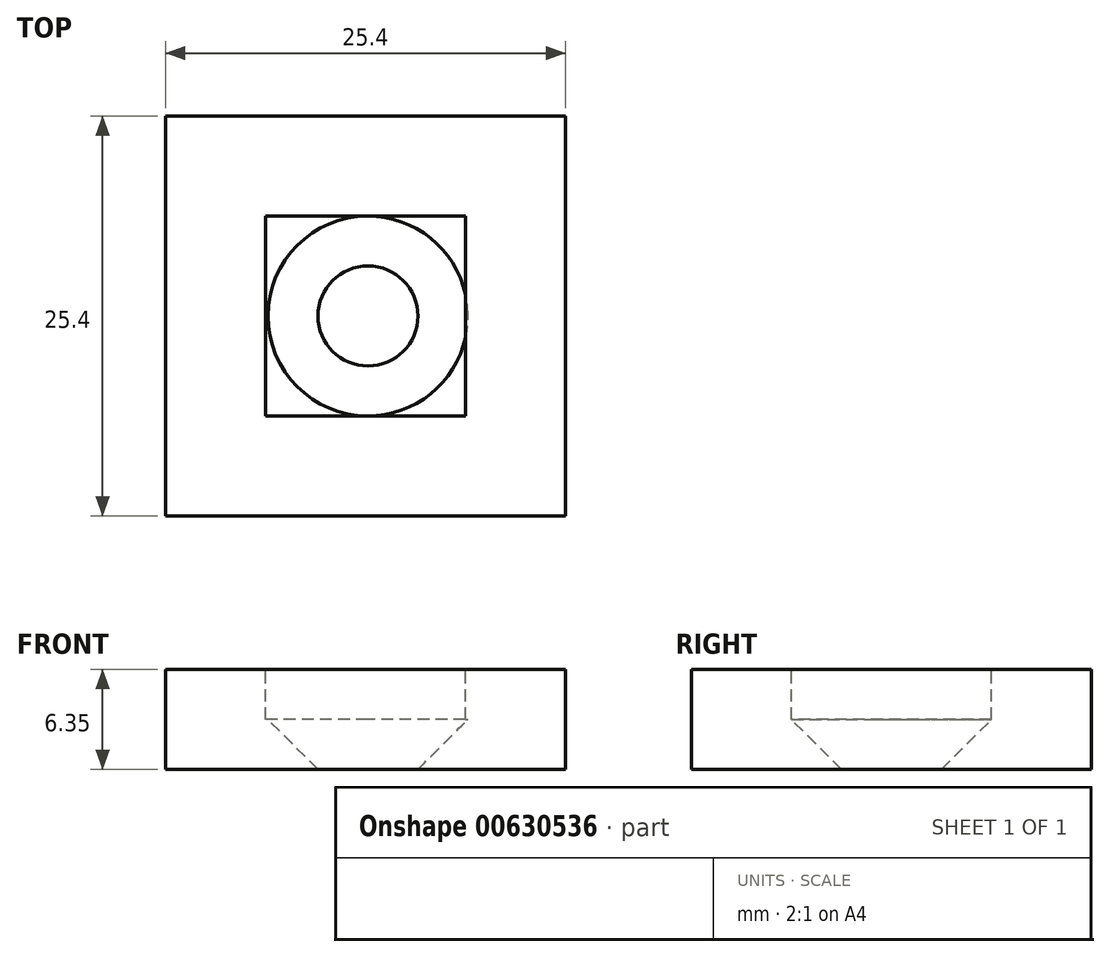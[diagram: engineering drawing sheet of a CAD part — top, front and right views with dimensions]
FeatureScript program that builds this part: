
annotation { "Feature Type Name" : "Feature", "Feature Type Description" : "" }
export const myFeature = defineFeature(function(context is Context, id is Id, definition is map)
    precondition{}
    {
        {
            var Q0;
            Q0=qCreatedBy(makeId("Top.planeOp"),FACE);
            var sketch = newSketch(context, id + "F0", { "sketchPlane" : qUnion([Q0])});
            skLineSegment(sketch, "E0.bottom", {"start": v(12.7, -12.7) * mm, "end": v(-12.7, -12.7) * mm});
            skLineSegment(sketch, "E0.top", {"start": v(12.7, 12.7) * mm, "end": v(-12.7, 12.7) * mm});
            skLineSegment(sketch, "E0.left", {"start": v(12.7, -12.7) * mm, "end": v(12.7, 12.7) * mm});
            skLineSegment(sketch, "E0.right", {"start": v(-12.7, -12.7) * mm, "end": v(-12.7, 12.7) * mm});
            skPoint(sketch, "E0.middle", {"position": v(0, 0) * mm});
            skSolve(sketch);
        }
        {
            var Q0;
            Q0 = qSketchRegion(id + "F0", true);
            extrude(context, id + "F1", {"entities" : qUnion([Q0]), "depth" : 6.35 * mm, "offsetDistance" : 25.4 * mm});
        }
        {
            var Q0;
            Q0=makeQuery(id+"F1.opExtrude","CAP_FACE",FACE,{"disambiguationData":[OSD([sQuery(id+"F0.wireOp",EDGE,"E0.bottom"),sQuery(id+"F0.wireOp",EDGE,"E0.top"),sQuery(id+"F0.wireOp",EDGE,"E0.left"),sQuery(id+"F0.wireOp",EDGE,"E0.right")])],"isStart":false});
            var sketch = newSketch(context, id + "F2", { "sketchPlane" : qUnion([Q0])});
            skLineSegment(sketch, "E1.bottom", {"start": v(6.35, -6.35) * mm, "end": v(-6.35, -6.35) * mm});
            skLineSegment(sketch, "E1.top", {"start": v(6.35, 6.35) * mm, "end": v(-6.35, 6.35) * mm});
            skLineSegment(sketch, "E1.left", {"start": v(6.35, -6.35) * mm, "end": v(6.35, 6.35) * mm});
            skLineSegment(sketch, "E1.right", {"start": v(-6.35, -6.35) * mm, "end": v(-6.35, 6.35) * mm});
            skPoint(sketch, "E1.middle", {"position": v(0, 0) * mm});
            skSolve(sketch);
        }
        {
            var Q0;
            Q0 = qSketchRegion(id + "F2", true);
            extrude(context, id + "F3", {"entities" : qUnion([Q0]), "operationType" : NewBodyOperationType.REMOVE, "oppositeDirection" : true, "depth" : 3.17 * mm, "offsetDistance" : 25.4 * mm});
        }
        {
            var Q0;
            Q0=makeQuery(id+"F3.boolean.opBoolean","COPY",FACE,{"derivedFrom":makeQuery(id+"F3.opExtrude","CAP_FACE",FACE,{"disambiguationData":[OSD([sQuery(id+"F2.wireOp",EDGE,"E1.bottom"),sQuery(id+"F2.wireOp",EDGE,"E1.top"),sQuery(id+"F2.wireOp",EDGE,"E1.left"),sQuery(id+"F2.wireOp",EDGE,"E1.right")])],"isStart":false})});
            var sketch = newSketch(context, id + "F4", { "sketchPlane" : qUnion([Q0])});
            skSolve(sketch);
        }
        {
            var Q0;
            Q0=makeQuery(id+"F4.imprint","IMPRINT",FACE,{"disambiguationData":[TD([[makeQuery(id+"F4.imprint","IMPRINT",EDGE,{"derivedFrom":makeQuery(id+"F3.boolean.opBoolean","COPY",EDGE,{"derivedFrom":makeQuery(id+"F3.opExtrude","CAP_EDGE",EDGE,{"disambiguationData":[OSD([sQuery(id+"F2.wireOp",EDGE,"E1.bottom")])],"isStart":false})})}),-1.0]])]});
            var sketch = newSketch(context, id + "F5", { "sketchPlane" : qUnion([Q0])});
            skCircle(sketch, "E2", {"center": v(0.15, 0) * mm, "radius": 0.18 * mm});
            skSolve(sketch);
        }
        {
            var Q0;
            Q0=sQuery(id+"F5.wireOp",VERTEX,"E2.center");
            var Q1;
            Q1=makeQuery(id+"F1.opExtrude","SWEPT_BODY",BODY,{"disambiguationData":[OSD([sQuery(id+"F0.wireOp",EDGE,"E0.bottom"),sQuery(id+"F0.wireOp",EDGE,"E0.top"),sQuery(id+"F0.wireOp",EDGE,"E0.left"),sQuery(id+"F0.wireOp",EDGE,"E0.right")])]});
            hole(context, id + "F6", {"style" : HoleStyle.C_SINK, "endStyle" : HoleEndStyle.BLIND, "holeDiameter" : 6.35 * mm, "cSinkDiameter" : 12.7 * mm, "cSinkAngle" : 90 * degree, "majorDiameter" : 6.35 * mm, "holeDepth" : 5.08 * mm, "isTappedThrough" : true, "tappedDepth" : 12.7 * mm, "tapClearance" : 3, "locations" : qUnion([Q0]), "scope" : qUnion([Q1])});
        }
    });
